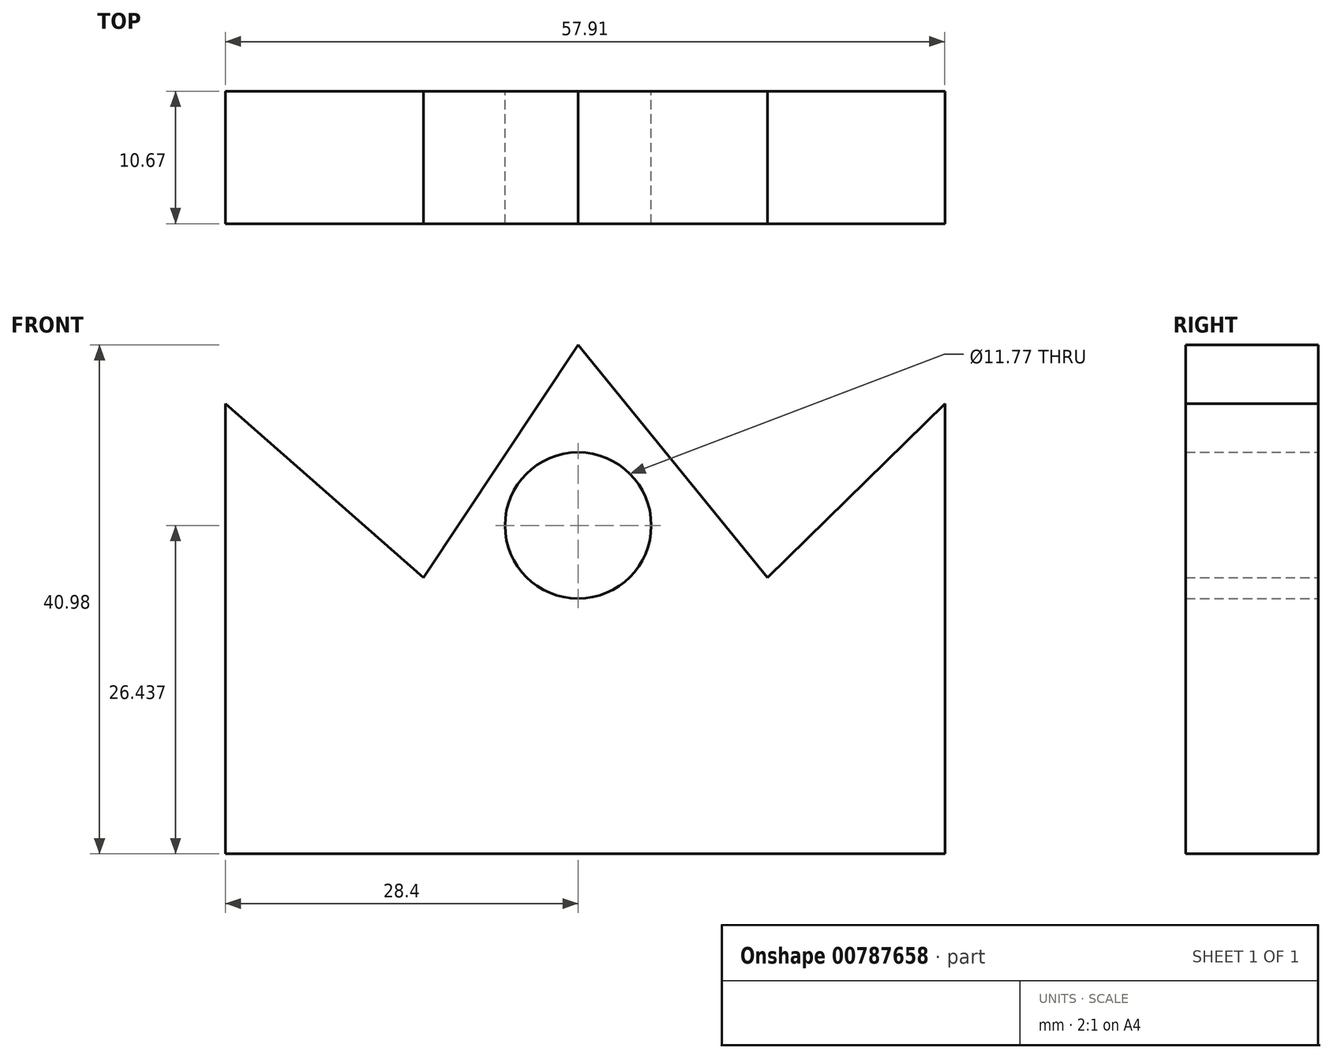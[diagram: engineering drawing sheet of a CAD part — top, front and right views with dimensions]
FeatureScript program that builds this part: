
annotation { "Feature Type Name" : "Feature", "Feature Type Description" : "" }
export const myFeature = defineFeature(function(context is Context, id is Id, definition is map)
    precondition{}
    {
        {
            var Q0;
            Q0=qCreatedBy(makeId("Front.planeOp"),FACE);
            var sketch = newSketch(context, id + "F0", { "sketchPlane" : qUnion([Q0])});
            skLineSegment(sketch, "E0", {"start": v(-28.4, 0) * mm, "end": v(29.51, 0) * mm});
            skLineSegment(sketch, "E1", {"start": v(29.51, 0) * mm, "end": v(29.51, 36.23) * mm});
            skLineSegment(sketch, "E2", {"start": v(29.51, 36.23) * mm, "end": v(15.25, 22.24) * mm});
            skLineSegment(sketch, "E3", {"start": v(15.25, 22.24) * mm, "end": v(0, 40.98) * mm});
            skLineSegment(sketch, "E4", {"start": v(0, 40.98) * mm, "end": v(-12.45, 22.24) * mm});
            skLineSegment(sketch, "E5", {"start": v(-12.45, 22.24) * mm, "end": v(-28.4, 36.23) * mm});
            skLineSegment(sketch, "E6", {"start": v(-28.4, 36.23) * mm, "end": v(-28.4, 0) * mm});
            skLineSegment(sketch, "E7", {"start": v(0, 40.98) * mm, "end": v(0, 51.9) * mm});
            skLineSegment(sketch, "E8", {"start": v(15.25, 22.24) * mm, "end": v(15.25, 38.19) * mm});
            skLineSegment(sketch, "E9", {"start": v(-12.45, 22.24) * mm, "end": v(-12.45, 38.19) * mm});
            skCircle(sketch, "E10", {"center": v(0, 26.44) * mm, "radius": 5.88 * mm});
            skSolve(sketch);
        }
        {
            var Q0;
            Q0=makeQuery(id+"F0.imprint","IMPRINT",FACE,{"disambiguationData":[TD([[makeQuery(id+"F0.imprint","IMPRINT",EDGE,{"derivedFrom":sQuery(id+"F0.wireOp",EDGE,"E0")}),1.0]])]});
            extrude(context, id + "F1", {"entities" : qUnion([Q0]), "depth" : 10.67 * mm, "offsetDistance" : 25.4 * mm});
        }
    });
